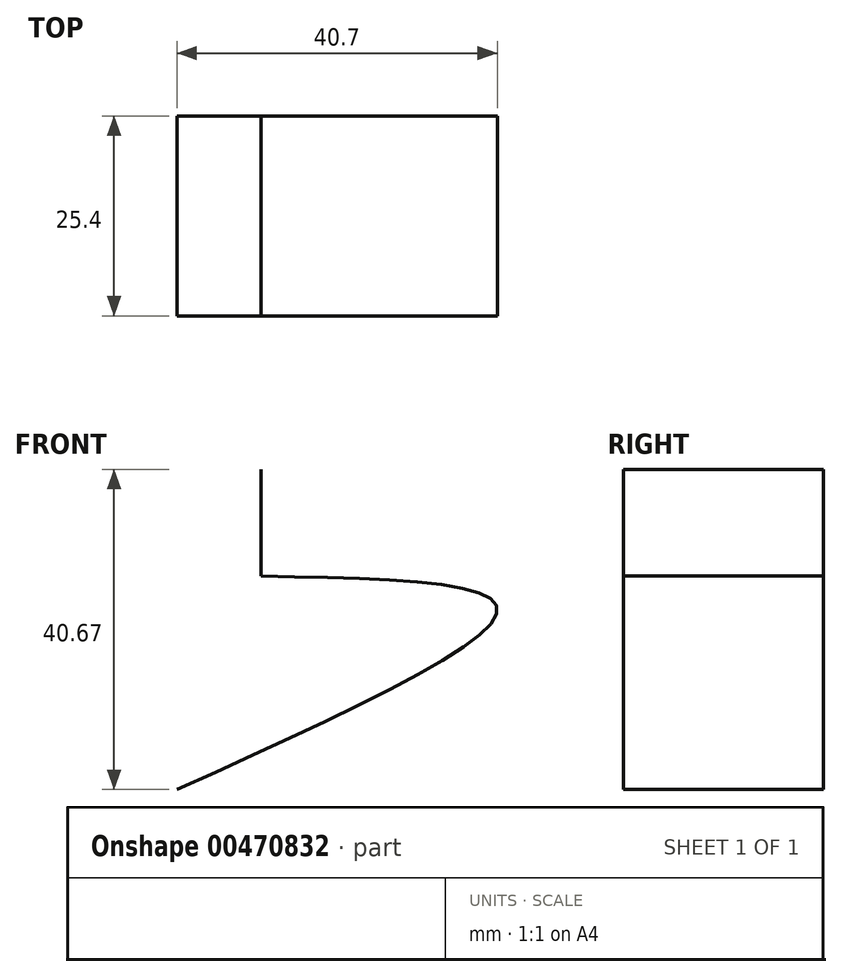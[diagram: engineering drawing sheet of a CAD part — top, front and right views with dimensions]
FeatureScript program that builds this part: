
annotation { "Feature Type Name" : "Feature", "Feature Type Description" : "" }
export const myFeature = defineFeature(function(context is Context, id is Id, definition is map)
    precondition{}
    {
        {
            var Q0;
            Q0=qCreatedBy(makeId("Front.planeOp"),FACE);
            var sketch = newSketch(context, id + "F0", { "sketchPlane" : qUnion([Q0])});
            skFitSpline(sketch, "E0", {"points": [v(2.22, 0) * mm, v(42.9, 23.11) * mm, v(12.9, 27.11) * mm], "startDerivative": vector(112.37, 50.78) * mm, "endDerivative": vector(-98.66, 1.68) * mm});
            skLineSegment(sketch, "E1", {"start": v(12.9, 27.11) * mm, "end": v(12.9, 40.67) * mm});
            skSolve(sketch);
        }
        {
            var Q0;
            Q0=sQuery(id+"F0.wireOp",EDGE,"E0");
            var Q1;
            Q1=sQuery(id+"F0.wireOp",EDGE,"E1");
            extrude(context, id + "F1", {"bodyType" : ToolBodyType.SURFACE, "surfaceEntities" : qUnion([Q0, Q1]), "depth" : 25.4 * mm});
        }
    });
